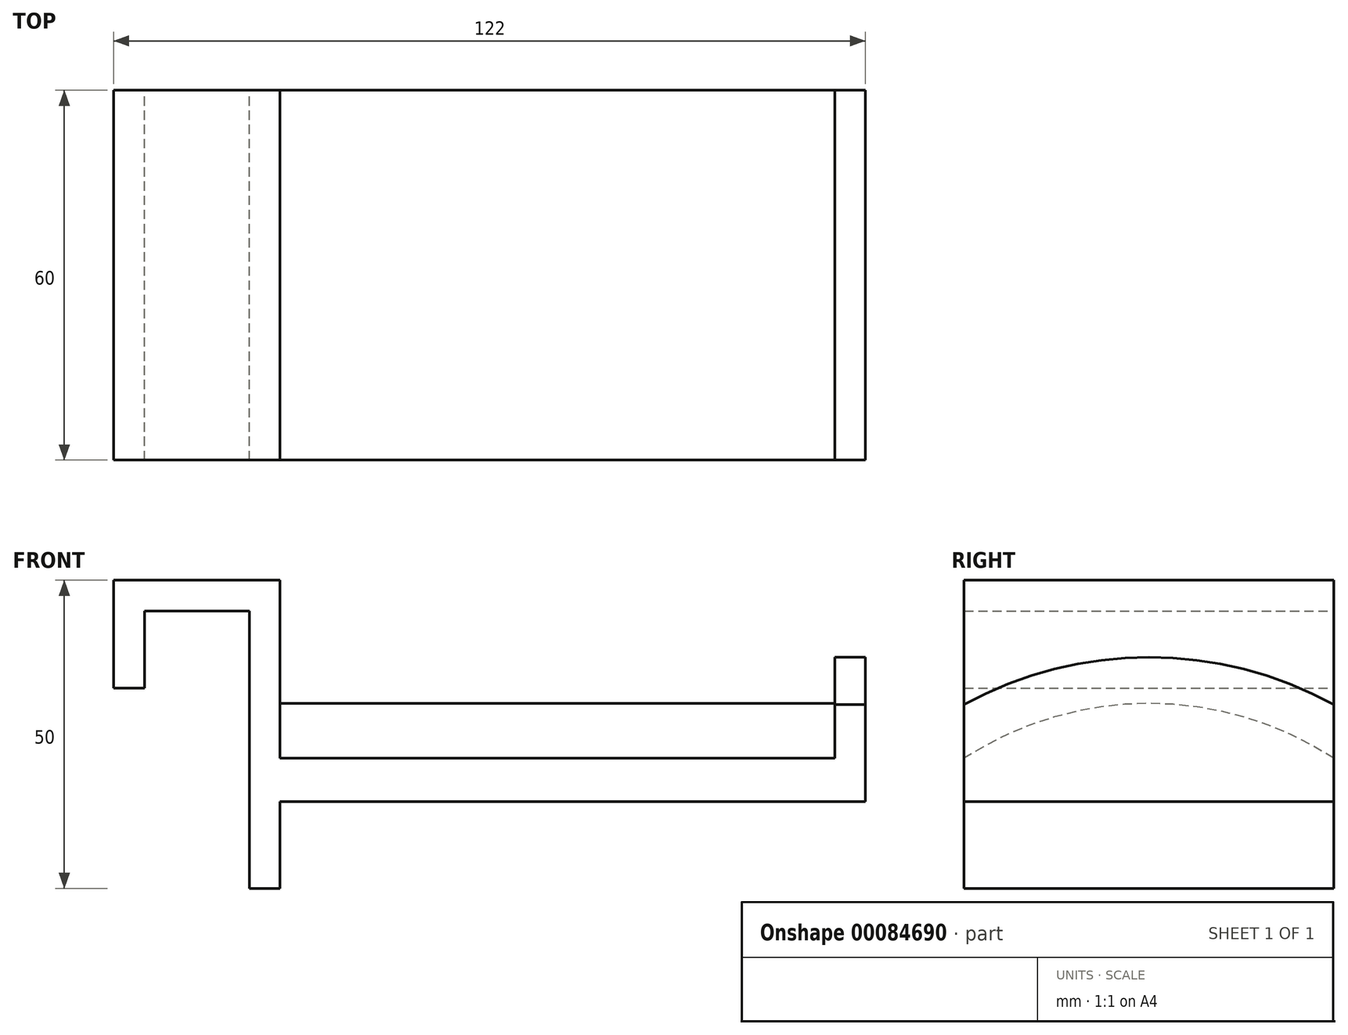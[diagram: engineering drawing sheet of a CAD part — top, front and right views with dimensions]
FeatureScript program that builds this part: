
annotation { "Feature Type Name" : "Feature", "Feature Type Description" : "" }
export const myFeature = defineFeature(function(context is Context, id is Id, definition is map)
    precondition{}
    {
        {
            var Q0;
            Q0=qCreatedBy(makeId("Front.planeOp"),FACE);
            var sketch = newSketch(context, id + "F0", { "sketchPlane" : qUnion([Q0])});
            skLineSegment(sketch, "E0", {"start": v(0, 0) * mm, "end": v(-5, 0) * mm});
            skLineSegment(sketch, "E1", {"start": v(-5, 0) * mm, "end": v(-5, 17.5) * mm});
            skLineSegment(sketch, "E2", {"start": v(-5, 17.5) * mm, "end": v(22, 17.5) * mm});
            skLineSegment(sketch, "E3", {"start": v(22, 17.5) * mm, "end": v(22, -32.5) * mm});
            skLineSegment(sketch, "E4", {"start": v(22, -32.5) * mm, "end": v(17, -32.5) * mm});
            skLineSegment(sketch, "E5", {"start": v(17, -32.5) * mm, "end": v(17, 12.5) * mm});
            skLineSegment(sketch, "E6", {"start": v(17, 12.5) * mm, "end": v(0, 12.5) * mm});
            skLineSegment(sketch, "E7", {"start": v(0, 12.5) * mm, "end": v(0, 0) * mm});
            skLineSegment(sketch, "E8", {"start": v(8.5, 17.5) * mm, "end": v(8.5, 12.5) * mm, "construction": true});
            skSolve(sketch);
        }
        {
            var Q0;
            Q0=makeQuery(id+"F0.imprint","IMPRINT",FACE,{"disambiguationData":[TD([[makeQuery(id+"F0.imprint","IMPRINT",EDGE,{"derivedFrom":sQuery(id+"F0.wireOp",EDGE,"E0")}),-1.0]])]});
            extrude(context, id + "F1", {"entities" : qUnion([Q0]), "depth" : 60 * mm});
        }
        {
            var Q0;
            Q0=makeQuery(id+"F1.opExtrude","SWEPT_FACE",FACE,{"disambiguationData":[OSD([sQuery(id+"F0.wireOp",EDGE,"E3")])]});
            var sketch = newSketch(context, id + "F2", { "sketchPlane" : qUnion([Q0])});
            skLineSegment(sketch, "E9.0.0", {"start": v(0, -32.5) * mm, "end": v(0, 17.5) * mm});
            skLineSegment(sketch, "E9.0.1", {"start": v(0, 17.5) * mm, "end": v(-60, 17.5) * mm});
            skLineSegment(sketch, "E9.0.2", {"start": v(-60, 17.5) * mm, "end": v(-60, -32.5) * mm});
            skLineSegment(sketch, "E9.0.3", {"start": v(-60, -32.5) * mm, "end": v(0, -32.5) * mm});
            skArc(sketch, "E10", {"start": v(0, -11.4) * mm, "mid": v(-30, -2.5) * mm, "end": v(-60, -11.4) * mm});
            skLineSegment(sketch, "E11", {"start": v(-30, 17.5) * mm, "end": v(-30, -2.5) * mm, "construction": true});
            skLineSegment(sketch, "E12", {"start": v(-60, -18.4) * mm, "end": v(0, -18.4) * mm});
            skSolve(sketch);
        }
        {
            var Q0;
            {var subQ0=sQuery(id+"F2.wireOp",EDGE,"E10");Q0=makeQuery(id+"F2.imprint","IMPRINT",FACE,{"disambiguationData":[TD([[makeQuery(id+"F2.imprint","IMPRINT",EDGE,{"derivedFrom":subQ0}),1.0]])]});}
            extrude(context, id + "F3", {"entities" : qUnion([Q0]), "operationType" : NewBodyOperationType.ADD, "depth" : 90 * mm});
        }
        {
            var Q0;
            Q0=makeQuery(id+"F3.opExtrude","CAP_FACE",FACE,{"disambiguationData":[OSD([sQuery(id+"F2.wireOp",EDGE,"E9.0.0"),sQuery(id+"F2.wireOp",EDGE,"E9.0.2"),sQuery(id+"F2.wireOp",EDGE,"E9.0.3"),sQuery(id+"F2.wireOp",EDGE,"E10")])],"isStart":false});
            var sketch = newSketch(context, id + "F4", { "sketchPlane" : qUnion([Q0])});
            skLineSegment(sketch, "E13.0.0", {"start": v(0, -18.4) * mm, "end": v(0, -11.4) * mm});
            skArc(sketch, "E13.0.1", {"start": v(0, -11.4) * mm, "mid": v(-30, -2.5) * mm, "end": v(-60, -11.4) * mm});
            skLineSegment(sketch, "E13.0.2", {"start": v(-60, -11.4) * mm, "end": v(-60, -18.4) * mm});
            skLineSegment(sketch, "E13.0.3", {"start": v(-60, -18.4) * mm, "end": v(0, -18.4) * mm});
            skArc(sketch, "E14.0", {"start": v(0, -2.67) * mm, "mid": v(-30, 5) * mm, "end": v(-60, -2.67) * mm});
            skLineSegment(sketch, "E15", {"start": v(-60, -2.67) * mm, "end": v(-60, -11.4) * mm});
            skLineSegment(sketch, "E16", {"start": v(0, -2.67) * mm, "end": v(0, -11.4) * mm});
            skSolve(sketch);
        }
        {
            var Q0;
            Q0=makeQuery(id+"F4.imprint","IMPRINT",FACE,{"disambiguationData":[TD([[makeQuery(id+"F4.imprint","IMPRINT",EDGE,{"derivedFrom":sQuery(id+"F4.wireOp",EDGE,"E13.0.1")}),-1.0]])]});
            var Q1;
            Q1=makeQuery(id+"F4.imprint","IMPRINT",FACE,{"disambiguationData":[TD([[makeQuery(id+"F4.imprint","IMPRINT",EDGE,{"derivedFrom":sQuery(id+"F4.wireOp",EDGE,"E13.0.0")}),-1.0]])]});
            extrude(context, id + "F5", {"entities" : qUnion([Q0, Q1]), "operationType" : NewBodyOperationType.ADD, "depth" : 5 * mm});
        }
    });
